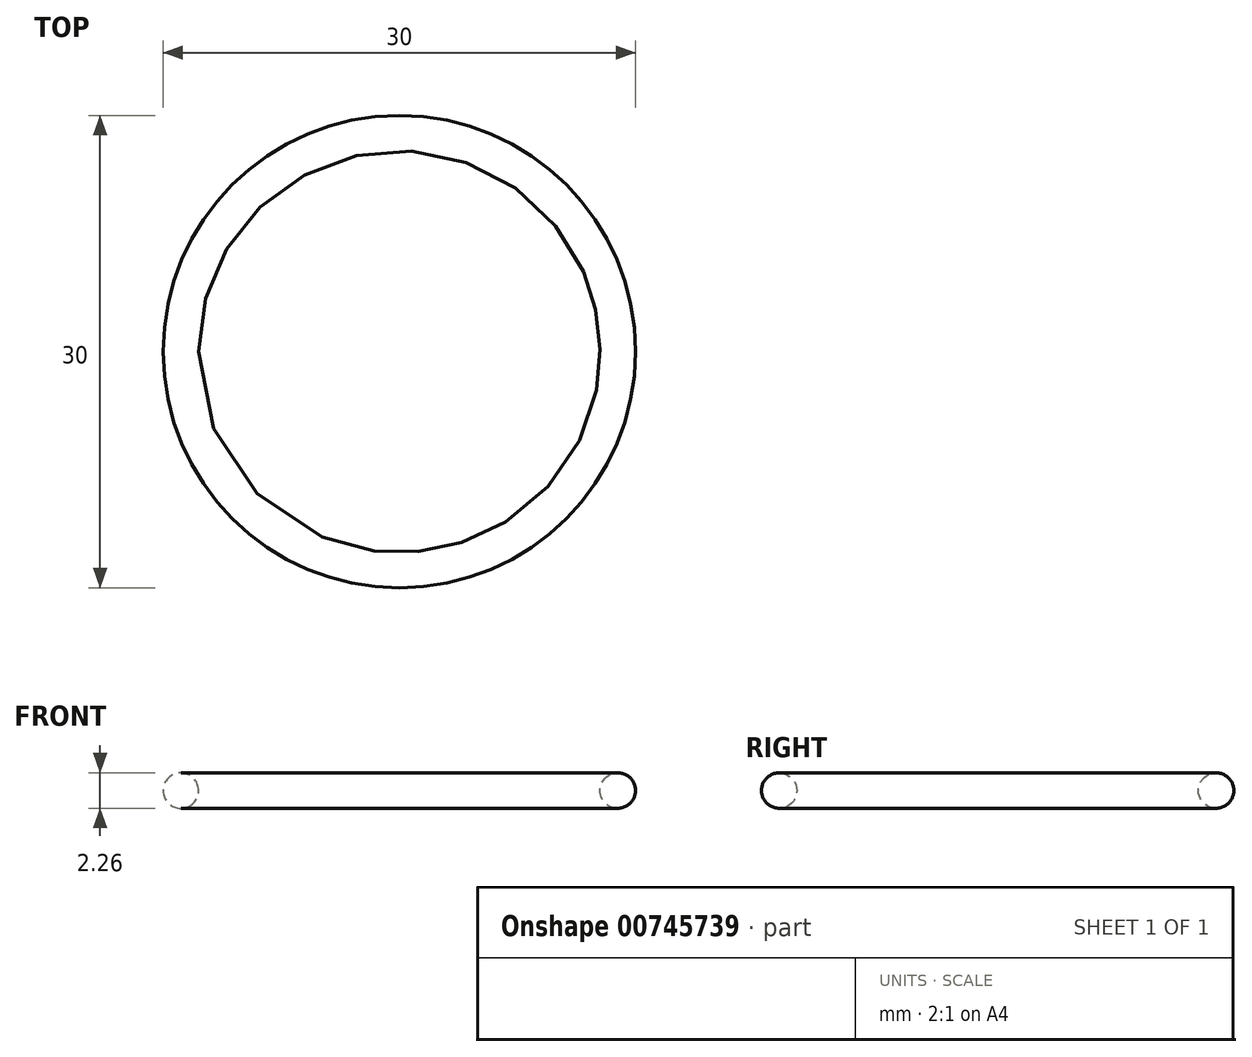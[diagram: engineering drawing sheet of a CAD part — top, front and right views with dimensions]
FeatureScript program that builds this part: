
annotation { "Feature Type Name" : "Feature", "Feature Type Description" : "" }
export const myFeature = defineFeature(function(context is Context, id is Id, definition is map)
    precondition{}
    {
        {
            var Q0;
            Q0=qCreatedBy(makeId("Front.planeOp"),FACE);
            var sketch = newSketch(context, id + "F0", { "sketchPlane" : qUnion([Q0])});
            skLineSegment(sketch, "E0", {"start": v(0, 0) * mm, "end": v(0, 10.24) * mm, "construction": true});
            skLineSegment(sketch, "E1", {"start": v(0, 0) * mm, "end": v(-13.88, 0) * mm, "construction": true});
            skLineSegment(sketch, "E2.bottom", {"start": v(-12.75, -1.12) * mm, "end": v(-15, -1.12) * mm, "construction": true});
            skLineSegment(sketch, "E2.top", {"start": v(-12.75, 1.12) * mm, "end": v(-15, 1.12) * mm, "construction": true});
            skLineSegment(sketch, "E2.left", {"start": v(-12.75, -1.12) * mm, "end": v(-12.75, 1.12) * mm, "construction": true});
            skLineSegment(sketch, "E2.right", {"start": v(-15, -1.12) * mm, "end": v(-15, 1.13) * mm, "construction": true});
            skPoint(sketch, "E2.middle", {"position": v(-13.88, 0) * mm});
            skCircle(sketch, "E3", {"center": v(-13.88, 0) * mm, "radius": 1.12 * mm});
            skSolve(sketch);
        }
        {
            var Q0;
            Q0 = qSketchRegion(id + "F0", true);
            var Q1;
            Q1=sQuery(id+"F0.wireOp",EDGE,"E0");
            revolve(context, id + "F1", {"surfaceOperationType" : NewSurfaceOperationType.NEW, "entities" : qUnion([Q0]), "axis" : qUnion([Q1]), "revolveType" : RevolveType.FULL});
        }
    });
